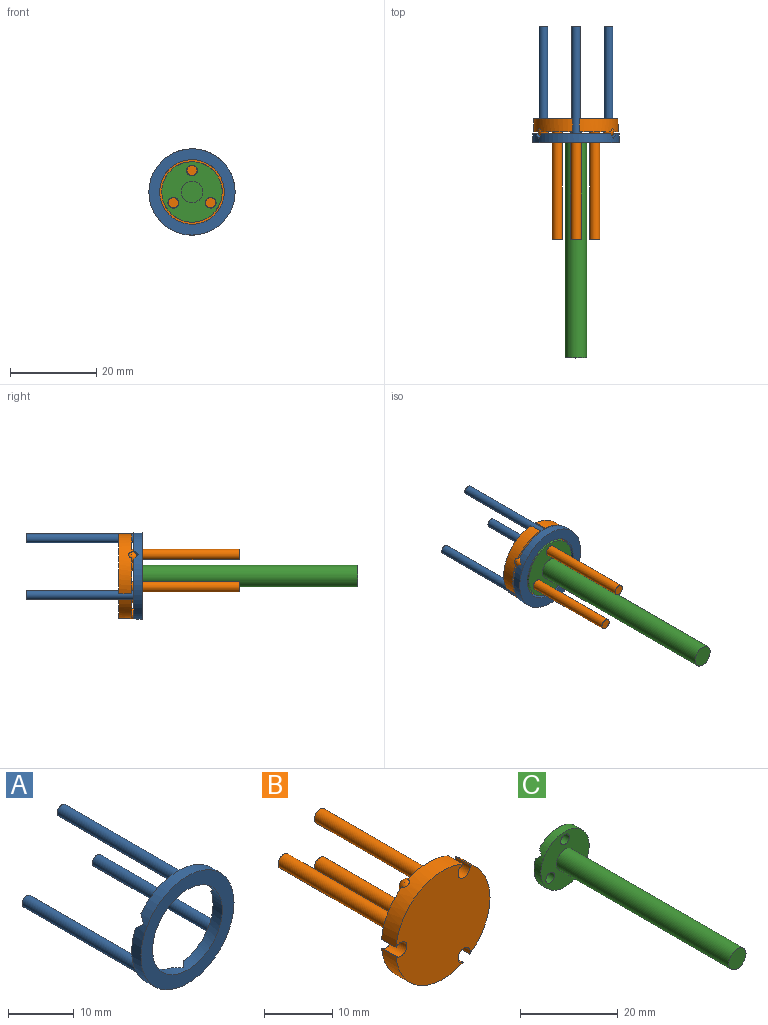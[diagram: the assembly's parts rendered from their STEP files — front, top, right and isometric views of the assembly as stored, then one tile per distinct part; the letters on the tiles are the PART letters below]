
ASSEMBLY  parts=3 mates=4
PART A: 18 faces, bbox 20x27x20 mm
  f0: cylinder r=7.5mm len=15mm, axis (0,1,0), area 89.9mm2, adj f2,f3,f4,f5,f6,f7,f8,f9
  f1: cylinder r=10mm len=20mm, axis (0,1,0), area 121.3mm2, adj f2,f3,f4,f5,f6,f7,f8,f9
  f2: plane 13.85x8.8mm, normal (0,1,0), area 36.7mm2, adj f0,f1,f6,f11,f14
  f3: plane 16x5.26mm, normal (0,1,0), area 36.7mm2, adj f0,f1,f9,f10,f12
  f4: plane 20x20mm, normal (0,-1,0), area 137.4mm2, adj f0,f1
  f5: plane 13.85x8.8mm, normal (0,1,0), area 36.7mm2, adj f0,f1,f7,f8,f16
  f6: plane 2.6x1.2mm, normal (-0.71,0.71,0), area 4.3mm2, adj f0,f1,f2,f7
  f7: plane 2.6x1.2mm, normal (0.71,0.71,0), area 4.3mm2, adj f0,f1,f5,f6
  f8: plane 2.71x2.34mm, normal (0.35,0.71,0.61), area 4.3mm2, adj f0,f1,f5,f9
  f9: plane 2.85x2.26mm, normal (-0.35,0.71,-0.61), area 4.3mm2, adj f0,f1,f3,f8
  f10: plane 2.85x2.26mm, normal (0.35,0.71,-0.61), area 4.3mm2, adj f0,f1,f3,f11
  f11: plane 2.71x2.34mm, normal (-0.35,0.71,0.61), area 4.3mm2, adj f0,f1,f2,f10
  f12: cylinder r=1mm len=25mm, axis (0,-1,0), area 157.1mm2, adj f3,f13
  f13: plane 2x2mm, normal (0,1,0), area 3.1mm2, adj f12
  f14: cylinder r=1mm len=25mm, axis (0,-1,0), area 157.1mm2, adj f2,f15
  f15: plane 2x2mm, normal (0,1,0), area 3.1mm2, adj f14
  f16: cylinder r=1mm len=25mm, axis (0,-1,0), area 157.1mm2, adj f5,f17
  f17: plane 2x2mm, normal (0,1,0), area 3.1mm2, adj f16
PART B: 20 faces, bbox 19.7x28x19.5 mm
  f0: cylinder r=9.75mm len=16.04mm, axis (0,1,0), area 55.8mm2, adj f2,f3,f5,f16,f19
  f1: cylinder r=9.75mm len=13.89mm, axis (0,1,0), area 55.8mm2, adj f2,f3,f6,f13,f19
  f2: plane 19.5x19.47mm, normal (0,-1,0), area 284.7mm2, adj f0,f1,f4,f13,f16,f19
  f3: plane 19.5x19.44mm, normal (0,1,0), area 245mm2, adj f0,f1,f4,f5,f6,f7,f8,f9
  f4: cylinder r=9.75mm len=13.89mm, axis (0,1,0), area 55.8mm2, adj f2,f3,f7,f13,f16
  f5: sphere r=1.2mm, area 9.8mm2, adj f0,f3
  f6: sphere r=1.2mm, area 9.8mm2, adj f1,f3
  f7: sphere r=1.2mm, area 9.8mm2, adj f3,f4
  f8: sphere r=1.2mm, area 9mm2, adj f3
  f9: sphere r=1.2mm, area 9mm2, adj f3
  f10: sphere r=1.2mm, area 9mm2, adj f3
  f11: cylinder r=1.18mm len=25mm, axis (0,-1,0), area 185.9mm2, adj f3,f12
  f12: plane 2.37x2.37mm, normal (0,1,0), area 4.4mm2, adj f11
  f13: cylinder r=1.25mm len=3mm, axis (0,1,0), area 18.4mm2, adj f1,f2,f3,f4
  f14: cylinder r=1.18mm len=25mm, axis (0,-1,0), area 185.9mm2, adj f3,f15
  f15: plane 2.37x2.37mm, normal (0,1,0), area 4.4mm2, adj f14
  f16: cylinder r=1.25mm len=3mm, axis (0,1,0), area 18.4mm2, adj f0,f2,f3,f4
  f17: cylinder r=1.18mm len=25mm, axis (0,-1,0), area 185.9mm2, adj f3,f18
  f18: plane 2.37x2.37mm, normal (0,1,0), area 4.4mm2, adj f17
  f19: cylinder r=1.25mm len=3mm, axis (0,1,0), area 18.4mm2, adj f0,f1,f2,f3
PART C: 18 faces, bbox 14x52x14 mm
  f0: cylinder r=7mm len=14mm, axis (0,1,0), area 83.6mm2, adj f1,f3,f4,f5,f6,f7,f8,f10
  f1: plane 9.31x5.8mm, normal (0,1,0), area 30.5mm2, adj f0,f3,f11,f12
  f2: cylinder r=1mm len=2mm, axis (0,1,0), area 8mm2, adj f3,f4,f6,f10,f12,f13,f17
  f3: plane 6.5x1.2mm, normal (-0.71,0.71,0), area 10.5mm2, adj f0,f1,f2,f6,f12
  f4: plane 6.07x3.99mm, normal (-0.35,0.71,-0.61), area 10.5mm2, adj f0,f2,f5,f10,f13
  f5: plane 10.75x5.61mm, normal (0,1,0), area 30.5mm2, adj f0,f4,f9,f13
  f6: plane 6.5x1.2mm, normal (0.71,0.71,0), area 10.5mm2, adj f0,f2,f3,f7,f10
  f7: plane 9.31x5.8mm, normal (0,1,0), area 30.5mm2, adj f0,f6,f10,f14
  f8: plane 14x14mm, normal (0,-1,0), area 119.6mm2, adj f0,f9,f11,f14,f16
  f9: cylinder r=1.25mm len=2.5mm, axis (0,1,0), area 15.7mm2, adj f5,f8
  f10: plane 5.71x4.2mm, normal (0.35,0.71,0.61), area 10.5mm2, adj f0,f2,f4,f6,f7
  f11: cylinder r=1.25mm len=2.5mm, axis (0,1,0), area 15.7mm2, adj f1,f8
  f12: plane 5.71x4.2mm, normal (-0.35,0.71,0.61), area 10.5mm2, adj f0,f1,f2,f3,f13
  f13: plane 6.07x3.99mm, normal (0.35,0.71,-0.61), area 10.5mm2, adj f0,f2,f4,f5,f12
  f14: cylinder r=1.25mm len=2.5mm, axis (0,1,0), area 15.7mm2, adj f7,f8
  f15: plane 5x5mm, normal (0,-1,0), area 19.6mm2, adj f16
  f16: cylinder r=2.5mm len=50mm, axis (0,1,0), area 785.4mm2, adj f8,f15
  f17: plane 2x2mm, normal (0,1,0), area 3.1mm2, adj f2
PLACE A at identity fixed
PLACE B rot(axis=(0.97,0,0.26),180deg) t=(0,0.52,0)mm
PLACE C rot(axis=(0,-1,0),120deg) t=(0,0.01,0)mm
MATE cylindrical C.f14 <-> B.f14  axis (0,1,0) through (4.33,0.01,-2.5)mm
MATE cylindrical B.f19 <-> A.f12  axis (0,-1,0) through (0,0.52,8.75)mm
MATE cylindrical C.f11 <-> B.f17  axis (0,1,0) through (0,0.01,5)mm
MATE cylindrical B.f16 <-> A.f14  axis (0,1,0) through (7.58,3.52,-4.37)mm
